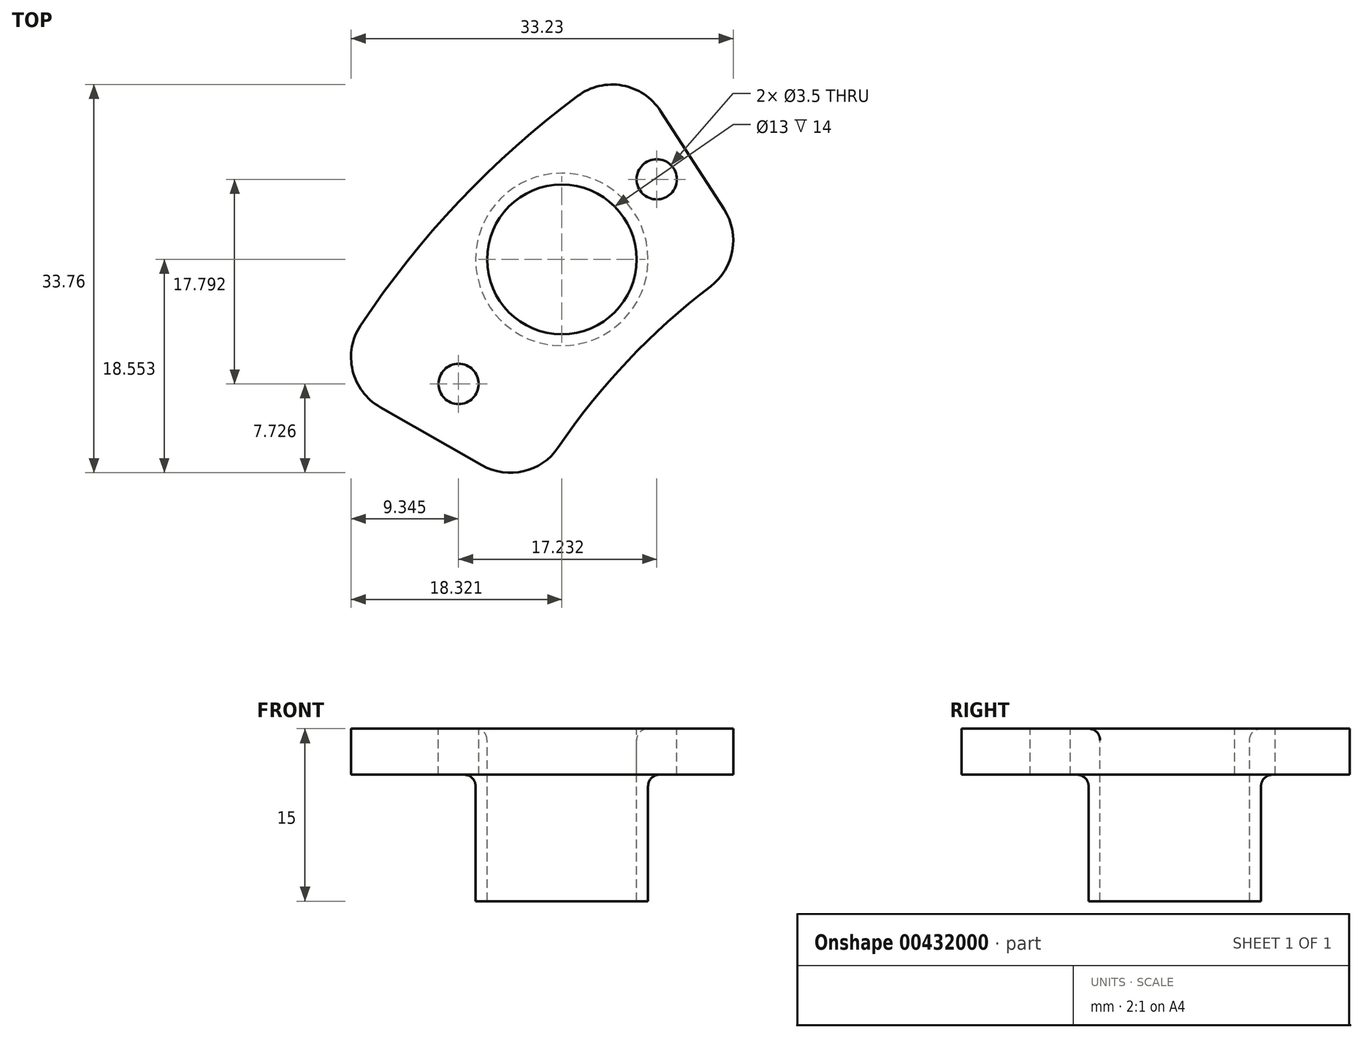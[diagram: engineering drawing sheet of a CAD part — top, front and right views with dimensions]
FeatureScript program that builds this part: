
annotation { "Feature Type Name" : "Feature", "Feature Type Description" : "" }
export const myFeature = defineFeature(function(context is Context, id is Id, definition is map)
    precondition{}
    {
        {
            var Q0;
            Q0=qCreatedBy(makeId("Top.planeOp"),FACE);
            var sketch = newSketch(context, id + "F0", { "sketchPlane" : qUnion([Q0])});
            skCircle(sketch, "E0", {"center": v(0, 0) * mm, "radius": 77.5 * mm});
            skCircle(sketch, "E1", {"center": v(0, 0) * mm, "radius": 76 * mm});
            skCircle(sketch, "E2", {"center": v(0, 0) * mm, "radius": 2.5 * mm});
            skLineSegment(sketch, "E3.bottom", {"start": v(0, 60) * mm, "end": v(-100, 60) * mm, "construction": true});
            skLineSegment(sketch, "E3.top", {"start": v(0, -60) * mm, "end": v(-100, -60) * mm, "construction": true});
            skLineSegment(sketch, "E3.left", {"start": v(0, 60) * mm, "end": v(0, -60) * mm, "construction": true});
            skLineSegment(sketch, "E3.right", {"start": v(-100, 60) * mm, "end": v(-100, -60) * mm, "construction": true});
            skCircle(sketch, "E4", {"center": v(0, 0) * mm, "radius": 87.5 * mm});
            skCircle(sketch, "E5", {"center": v(0, 0) * mm, "radius": 62.5 * mm});
            skLineSegment(sketch, "E6", {"start": v(0, 0) * mm, "end": v(-84.15, 101.51) * mm, "construction": true});
            skLineSegment(sketch, "E7", {"start": v(-55.84, 67.36) * mm, "end": v(-48.5, 58.5) * mm});
            skCircle(sketch, "E8", {"center": v(-49.13, 49.86) * mm, "radius": 6.5 * mm});
            skArc(sketch, "E9", {"start": v(-55.84, 67.36) * mm, "mid": v(-47.75, 69.99) * mm, "end": v(-40.08, 66.33) * mm});
            skLineSegment(sketch, "E10", {"start": v(0, 0) * mm, "end": v(-47.48, 73.5) * mm, "construction": true});
            skLineSegment(sketch, "E11", {"start": v(-43.36, 67.12) * mm, "end": v(-33.91, 52.5) * mm});
            skLineSegment(sketch, "E12", {"start": v(-32.4, 50.17) * mm, "end": v(-33.91, 52.5) * mm});
            skCircle(sketch, "E13", {"center": v(-49.13, 49.86) * mm, "radius": 7.5 * mm});
            skLineSegment(sketch, "E14", {"start": v(0, 0) * mm, "end": v(-76.01, 43.34) * mm, "construction": true});
            skArc(sketch, "E15", {"start": v(-43.36, 67.12) * mm, "mid": v(-58.05, 54.92) * mm, "end": v(-69.42, 39.58) * mm});
            skArc(sketch, "E16", {"start": v(-32.4, 50.17) * mm, "mid": v(-43.39, 41.05) * mm, "end": v(-51.89, 29.58) * mm});
            skLineSegment(sketch, "E17", {"start": v(-69.42, 39.58) * mm, "end": v(-51.89, 29.58) * mm});
            skCircle(sketch, "E18", {"center": v(0, 0) * mm, "radius": 70 * mm, "construction": true});
            skCircle(sketch, "E19", {"center": v(-58.1, 39.04) * mm, "radius": 1.75 * mm});
            skCircle(sketch, "E20", {"center": v(-40.87, 56.83) * mm, "radius": 1.75 * mm});
            skSolve(sketch);
        }
        {
            var Q0;
            {var subQ6=sQuery(id+"F0.wireOp",EDGE,"E1");var subQ9=makeQuery(id+"F0.imprint","INTERSECT",VERTEX,{"derivedFrom":[subQ6,sQuery(id+"F0.wireOp",EDGE,"E7")]});Q0=makeQuery(id+"F0.imprint","IMPRINT",FACE,{"disambiguationData":[TD([[makeQuery(id+"F0.imprint","IMPRINT",EDGE,{"disambiguationData":[TD([[subQ9,1.0]])],"derivedFrom":subQ6}),1.0]])]});}
            var Q1;
            {var subQ0=sQuery(id+"F0.wireOp",EDGE,"E7");var subQ3=sQuery(id+"F0.wireOp",EDGE,"E0");var subQ4=makeQuery(id+"F0.imprint","INTERSECT",VERTEX,{"derivedFrom":[subQ3,subQ0]});Q1=makeQuery(id+"F0.imprint","IMPRINT",FACE,{"disambiguationData":[TD([[makeQuery(id+"F0.imprint","IMPRINT",EDGE,{"disambiguationData":[TD([[subQ4,-1.0]])],"derivedFrom":subQ3}),1.0]])]});}
            var Q2;
            {var subQ0=sQuery(id+"F0.wireOp",EDGE,"E7");var subQ1=sQuery(id+"F0.wireOp",EDGE,"E0");var subQ2=makeQuery(id+"F0.imprint","INTERSECT",VERTEX,{"derivedFrom":[subQ1,subQ0]});Q2=makeQuery(id+"F0.imprint","IMPRINT",FACE,{"disambiguationData":[TD([[makeQuery(id+"F0.imprint","IMPRINT",EDGE,{"disambiguationData":[TD([[subQ2,-1.0]])],"derivedFrom":subQ1}),-1.0]])]});}
            var Q3;
            {var subQ0=sQuery(id+"F0.wireOp",EDGE,"E11");var subQ1=sQuery(id+"F0.wireOp",EDGE,"E0");var subQ2=makeQuery(id+"F0.imprint","INTERSECT",VERTEX,{"derivedFrom":[subQ1,subQ0]});Q3=makeQuery(id+"F0.imprint","IMPRINT",FACE,{"disambiguationData":[TD([[makeQuery(id+"F0.imprint","IMPRINT",EDGE,{"disambiguationData":[TD([[subQ2,-1.0]])],"derivedFrom":subQ1}),-1.0]])]});}
            var Q4;
            {var subQ0=sQuery(id+"F0.wireOp",EDGE,"E11");var subQ1=sQuery(id+"F0.wireOp",EDGE,"E0");var subQ2=makeQuery(id+"F0.imprint","INTERSECT",VERTEX,{"derivedFrom":[subQ1,subQ0]});Q4=makeQuery(id+"F0.imprint","IMPRINT",FACE,{"disambiguationData":[TD([[makeQuery(id+"F0.imprint","IMPRINT",EDGE,{"disambiguationData":[TD([[subQ2,-1.0]])],"derivedFrom":subQ1}),1.0]])]});}
            var Q5;
            Q5=makeQuery(id+"F0.imprint","IMPRINT",FACE,{"disambiguationData":[TD([[makeQuery(id+"F0.imprint","IMPRINT",EDGE,{"derivedFrom":sQuery(id+"F0.wireOp",EDGE,"WrZBJqnl-nBdy-o6x2-8oXG-Tt0npwXfaI6l")}),1.0]])]});
            var Q6;
            {var subQ0=sQuery(id+"F0.wireOp",EDGE,"E13");var subQ1=sQuery(id+"F0.wireOp",EDGE,"E0");var subQ2=makeQuery(id+"F0.imprint","INTERSECT",VERTEX,{"derivedFrom":[subQ1,subQ0]});Q6=makeQuery(id+"F0.imprint","IMPRINT",FACE,{"disambiguationData":[TD([[makeQuery(id+"F0.imprint","IMPRINT",EDGE,{"disambiguationData":[TD([[subQ2,-1.0]])],"derivedFrom":subQ1}),1.0]])]});}
            var Q7;
            {var subQ1=sQuery(id+"F0.wireOp",EDGE,"E1");var subQ4=sQuery(id+"F0.wireOp",EDGE,"E13");var subQ7=makeQuery(id+"F0.imprint","INTERSECT",VERTEX,{"disambiguationData":[OD(0.0)],"derivedFrom":[subQ1,subQ4]});Q7=makeQuery(id+"F0.imprint","IMPRINT",FACE,{"disambiguationData":[TD([[makeQuery(id+"F0.imprint","IMPRINT",EDGE,{"disambiguationData":[TD([[subQ7,-1.0]])],"derivedFrom":subQ1}),-1.0]])]});}
            var Q8;
            {var subQ0=sQuery(id+"F0.wireOp",EDGE,"E13");var subQ1=sQuery(id+"F0.wireOp",EDGE,"E1");var subQ7=makeQuery(id+"F0.imprint","INTERSECT",VERTEX,{"disambiguationData":[OD(0.0)],"derivedFrom":[subQ1,subQ0]});Q8=makeQuery(id+"F0.imprint","IMPRINT",FACE,{"disambiguationData":[TD([[makeQuery(id+"F0.imprint","IMPRINT",EDGE,{"disambiguationData":[TD([[subQ7,-1.0]])],"derivedFrom":subQ1}),1.0]])]});}
            var Q9;
            {var subQ0=sQuery(id+"F0.wireOp",EDGE,"E13");var subQ1=sQuery(id+"F0.wireOp",EDGE,"E1");var subQ2=makeQuery(id+"F0.imprint","INTERSECT",VERTEX,{"disambiguationData":[OD(1.0)],"derivedFrom":[subQ1,subQ0]});Q9=makeQuery(id+"F0.imprint","IMPRINT",FACE,{"disambiguationData":[TD([[makeQuery(id+"F0.imprint","IMPRINT",EDGE,{"disambiguationData":[TD([[subQ2,-1.0]])],"derivedFrom":subQ1}),1.0]])]});}
            var Q10;
            {var subQ1=sQuery(id+"F0.wireOp",EDGE,"E12");Q10=makeQuery(id+"F0.imprint","IMPRINT",FACE,{"disambiguationData":[TD([[makeQuery(id+"F0.imprint","IMPRINT",EDGE,{"derivedFrom":subQ1}),1.0]])]});}
            extrude(context, id + "F1", {"entities" : qUnion([Q0, Q1, Q2, Q3, Q4, Q5, Q6, Q7, Q8, Q9, Q10]), "oppositeDirection" : true, "depth" : 4 * mm, "offsetDistance" : 25 * mm});
        }
        {
            var Q0;
            {var subQ1=sQuery(id+"F0.wireOp",EDGE,"E1");var subQ4=sQuery(id+"F0.wireOp",EDGE,"E13");var subQ7=makeQuery(id+"F0.imprint","INTERSECT",VERTEX,{"disambiguationData":[OD(0.0)],"derivedFrom":[subQ1,subQ4]});Q0=makeQuery(id+"F0.imprint","IMPRINT",FACE,{"disambiguationData":[TD([[makeQuery(id+"F0.imprint","IMPRINT",EDGE,{"disambiguationData":[TD([[subQ7,-1.0]])],"derivedFrom":subQ1}),-1.0]])]});}
            var Q1;
            {var subQ0=sQuery(id+"F0.wireOp",EDGE,"E13");var subQ1=sQuery(id+"F0.wireOp",EDGE,"E1");var subQ7=makeQuery(id+"F0.imprint","INTERSECT",VERTEX,{"disambiguationData":[OD(0.0)],"derivedFrom":[subQ1,subQ0]});Q1=makeQuery(id+"F0.imprint","IMPRINT",FACE,{"disambiguationData":[TD([[makeQuery(id+"F0.imprint","IMPRINT",EDGE,{"disambiguationData":[TD([[subQ7,-1.0]])],"derivedFrom":subQ1}),1.0]])]});}
            var Q2;
            Q2=sQuery(id+"F0.wireOp",EDGE,"E13");
            var Q3;
            Q3=sQuery(id+"F0.wireOp",EDGE,"E8");
            extrude(context, id + "F2", {"entities" : qUnion([Q0, Q1]), "operationType" : NewBodyOperationType.ADD, "surfaceEntities" : qUnion([Q2, Q3]), "oppositeDirection" : true, "depth" : 15 * mm, "offsetDistance" : 25 * mm});
        }
        {
            var Q0;
            Q0=makeQuery(id+"F1.opExtrude","SWEPT_EDGE",EDGE,{"disambiguationData":[OSD([sQuery(id+"F0.wireOp",EDGE,"dcUFn44s-pDy7-Tfzy-h6N0-xDkfoGxMLKwH"),sQuery(id+"F0.wireOp",EDGE,"E11")])]});
            var Q1;
            Q1=makeQuery(id+"F1.opExtrude","SWEPT_EDGE",EDGE,{"disambiguationData":[OSD([sQuery(id+"F0.wireOp",EDGE,"WrZBJqnl-nBdy-o6x2-8oXG-Tt0npwXfaI6l"),sQuery(id+"F0.wireOp",EDGE,"E12")])]});
            var Q2;
            Q2=makeQuery(id+"F1.opExtrude","SWEPT_EDGE",EDGE,{"disambiguationData":[OSD([sQuery(id+"F0.wireOp",EDGE,"WrZBJqnl-nBdy-o6x2-8oXG-Tt0npwXfaI6l"),sQuery(id+"F0.wireOp",EDGE,"mklulyK3-P0Q5-E4vQ-XCCq-23Wyug4wNRz8")])]});
            var Q3;
            Q3=makeQuery(id+"F1.opExtrude","SWEPT_EDGE",EDGE,{"disambiguationData":[OSD([sQuery(id+"F0.wireOp",EDGE,"dcUFn44s-pDy7-Tfzy-h6N0-xDkfoGxMLKwH"),sQuery(id+"F0.wireOp",EDGE,"SK3dnNe3-XBkn-8xfK-P51F-xpqPZoGmj958")])]});
            var Q4;
            Q4=makeQuery(id+"F1.opExtrude","SWEPT_EDGE",EDGE,{"disambiguationData":[OSD([sQuery(id+"F0.wireOp",EDGE,"E5"),sQuery(id+"F0.wireOp",EDGE,"E17")])]});
            var Q5;
            Q5=makeQuery(id+"F1.opExtrude","SWEPT_EDGE",EDGE,{"disambiguationData":[OSD([sQuery(id+"F0.wireOp",EDGE,"E15"),sQuery(id+"F0.wireOp",EDGE,"E17")])]});
            fillet(context, id + "F3", {"entities" : qUnion([Q0, Q1, Q2, Q3, Q4, Q5]), "radius" : 5 * mm, "tangentPropagation" : true, "allowEdgeOverflow" : false});
        }
        {
            var Q0;
            Q0=makeQuery(id+"F2.boolean.opBoolean","INTERSECT",EDGE,{"derivedFrom":[makeQuery(id+"F1.opExtrude","CAP_FACE",FACE,{"disambiguationData":[OSD([sQuery(id+"F0.wireOp",EDGE,"E8"),sQuery(id+"F0.wireOp",EDGE,"dcUFn44s-pDy7-Tfzy-h6N0-xDkfoGxMLKwH"),sQuery(id+"F0.wireOp",EDGE,"SK3dnNe3-XBkn-8xfK-P51F-xpqPZoGmj958"),sQuery(id+"F0.wireOp",EDGE,"E11"),sQuery(id+"F0.wireOp",EDGE,"WrZBJqnl-nBdy-o6x2-8oXG-Tt0npwXfaI6l"),sQuery(id+"F0.wireOp",EDGE,"mklulyK3-P0Q5-E4vQ-XCCq-23Wyug4wNRz8"),sQuery(id+"F0.wireOp",EDGE,"E12")])],"isStart":false}),makeQuery(id+"F2.opExtrude","SWEPT_FACE",FACE,{"disambiguationData":[OSD([sQuery(id+"F0.wireOp",EDGE,"E13")])]})]});
            var Q1;
            Q1=makeQuery(id+"F1.opExtrude","CAP_EDGE",EDGE,{"disambiguationData":[OSD([sQuery(id+"F0.wireOp",EDGE,"E8")])],"isStart":true});
            fillet(context, id + "F4", {"entities" : qUnion([Q0, Q1]), "radius" : 1 * mm, "tangentPropagation" : true, "allowEdgeOverflow" : false});
        }
    });
